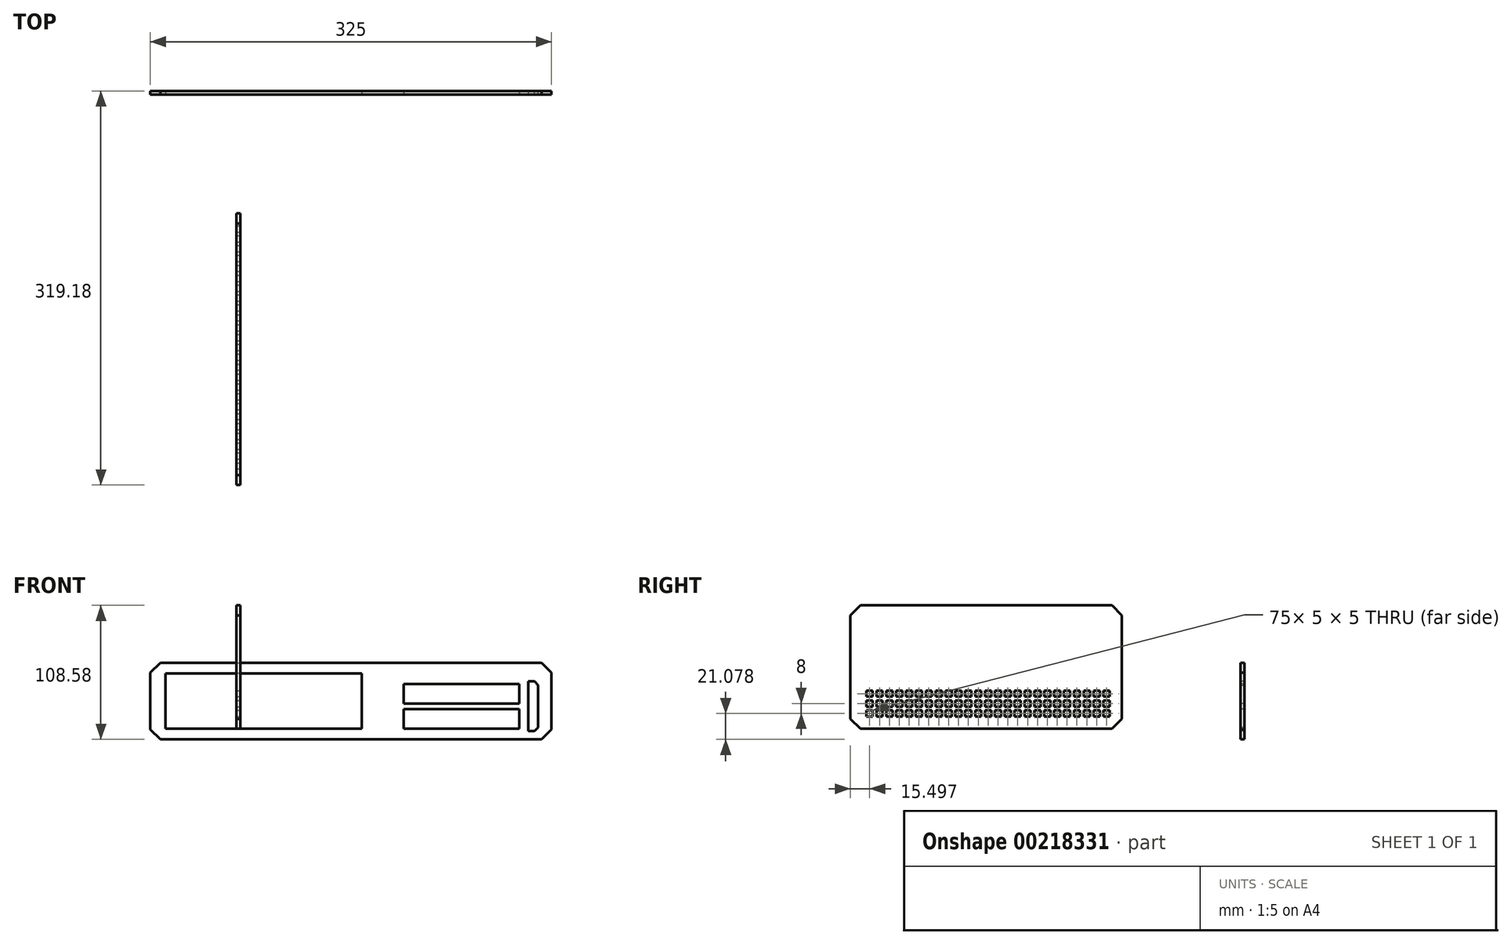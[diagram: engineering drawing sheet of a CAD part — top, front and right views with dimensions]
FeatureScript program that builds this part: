
annotation { "Feature Type Name" : "Feature", "Feature Type Description" : "" }
export const myFeature = defineFeature(function(context is Context, id is Id, definition is map)
    precondition{}
    {
        {
            var Q0;
            Q0=qCreatedBy(makeId("Front.planeOp"),FACE);
            var sketch = newSketch(context, id + "F0", { "sketchPlane" : qUnion([Q0])});
            skLineSegment(sketch, "E0.bottom", {"start": v(-69.82, 57.21) * mm, "end": v(255.18, 57.21) * mm});
            skLineSegment(sketch, "E0.top", {"start": v(-69.82, -4.79) * mm, "end": v(255.18, -4.79) * mm});
            skLineSegment(sketch, "E0.left", {"start": v(-69.82, 57.21) * mm, "end": v(-69.82, -4.79) * mm});
            skLineSegment(sketch, "E0.right", {"start": v(255.18, 57.21) * mm, "end": v(255.18, -4.79) * mm});
            skSolve(sketch);
        }
        {
            var Q0;
            Q0=makeQuery(id+"F0.imprint","IMPRINT",FACE,{"disambiguationData":[TD([[makeQuery(id+"F0.imprint","IMPRINT",EDGE,{"derivedFrom":sQuery(id+"F0.wireOp",EDGE,"E0.bottom")}),-1.0]])]});
            extrude(context, id + "F1", {"entities" : qUnion([Q0]), "depth" : 3 * mm});
        }
        {
            var Q0;
            Q0=qCreatedBy(makeId("Right.planeOp"),FACE);
            var sketch = newSketch(context, id + "F2", { "sketchPlane" : qUnion([Q0])});
            skLineSegment(sketch, "E1.bottom", {"start": v(-319.18, 103.79) * mm, "end": v(-99.18, 103.79) * mm});
            skLineSegment(sketch, "E1.top", {"start": v(-319.18, 3.79) * mm, "end": v(-99.18, 3.79) * mm});
            skLineSegment(sketch, "E1.left", {"start": v(-319.18, 103.79) * mm, "end": v(-319.18, 3.79) * mm});
            skLineSegment(sketch, "E1.right", {"start": v(-99.18, 103.79) * mm, "end": v(-99.18, 3.79) * mm});
            skSolve(sketch);
        }
        {
            var Q0;
            Q0=makeQuery(id+"F2.imprint","IMPRINT",FACE,{"disambiguationData":[TD([[makeQuery(id+"F2.imprint","IMPRINT",EDGE,{"derivedFrom":sQuery(id+"F2.wireOp",EDGE,"E1.bottom")}),-1.0]])]});
            extrude(context, id + "F3", {"entities" : qUnion([Q0]), "depth" : 3 * mm});
        }
        {
            var Q0;
            Q0=makeQuery(id+"F1.opExtrude","SWEPT_EDGE",EDGE,{"disambiguationData":[OSD([sQuery(id+"F0.wireOp",EDGE,"E0.bottom"),sQuery(id+"F0.wireOp",EDGE,"E0.left")])]});
            var Q1;
            Q1=makeQuery(id+"F1.opExtrude","SWEPT_EDGE",EDGE,{"disambiguationData":[OSD([sQuery(id+"F0.wireOp",EDGE,"E0.top"),sQuery(id+"F0.wireOp",EDGE,"E0.left")])]});
            var Q2;
            Q2=makeQuery(id+"F1.opExtrude","SWEPT_EDGE",EDGE,{"disambiguationData":[OSD([sQuery(id+"F0.wireOp",EDGE,"E0.bottom"),sQuery(id+"F0.wireOp",EDGE,"E0.right")])]});
            var Q3;
            Q3=makeQuery(id+"F1.opExtrude","SWEPT_EDGE",EDGE,{"disambiguationData":[OSD([sQuery(id+"F0.wireOp",EDGE,"E0.top"),sQuery(id+"F0.wireOp",EDGE,"E0.right")])]});
            var Q4;
            Q4=makeQuery(id+"F3.opExtrude","SWEPT_EDGE",EDGE,{"disambiguationData":[OSD([sQuery(id+"F2.wireOp",EDGE,"E1.bottom"),sQuery(id+"F2.wireOp",EDGE,"E1.left")])]});
            var Q5;
            Q5=makeQuery(id+"F3.opExtrude","SWEPT_EDGE",EDGE,{"disambiguationData":[OSD([sQuery(id+"F2.wireOp",EDGE,"E1.top"),sQuery(id+"F2.wireOp",EDGE,"E1.left")])]});
            var Q6;
            Q6=makeQuery(id+"F3.opExtrude","SWEPT_EDGE",EDGE,{"disambiguationData":[OSD([sQuery(id+"F2.wireOp",EDGE,"E1.top"),sQuery(id+"F2.wireOp",EDGE,"E1.right")])]});
            var Q7;
            Q7=makeQuery(id+"F3.opExtrude","SWEPT_EDGE",EDGE,{"disambiguationData":[OSD([sQuery(id+"F2.wireOp",EDGE,"E1.bottom"),sQuery(id+"F2.wireOp",EDGE,"E1.right")])]});
            chamfer(context, id + "F4", {"entities" : qUnion([Q0, Q1, Q2, Q3, Q4, Q5, Q6, Q7]), "width" : 8 * mm, "tangentPropagation" : true});
        }
        {
            var Q0;
            Q0=makeQuery(id+"F1.opExtrude","CAP_FACE",FACE,{"disambiguationData":[OSD([sQuery(id+"F0.wireOp",EDGE,"E0.bottom"),sQuery(id+"F0.wireOp",EDGE,"E0.top"),sQuery(id+"F0.wireOp",EDGE,"E0.left"),sQuery(id+"F0.wireOp",EDGE,"E0.right")])],"isStart":false});
            var sketch = newSketch(context, id + "F5", { "sketchPlane" : qUnion([Q0])});
            skLineSegment(sketch, "E2", {"start": v(-54.82, -4.79) * mm, "end": v(-54.82, 8.21) * mm, "construction": true});
            skLineSegment(sketch, "E3", {"start": v(-54.82, 8.21) * mm, "end": v(115.18, 8.21) * mm, "construction": true});
            skLineSegment(sketch, "E4", {"start": v(115.18, 8.21) * mm, "end": v(115.18, 4) * mm, "construction": true});
            skLineSegment(sketch, "E5", {"start": v(115.18, 4) * mm, "end": v(101.58, 4) * mm, "construction": true});
            skLineSegment(sketch, "E6.bottom", {"start": v(101.58, 4) * mm, "end": v(-57.42, 4) * mm});
            skLineSegment(sketch, "E6.top", {"start": v(101.58, 48.7) * mm, "end": v(-57.42, 48.7) * mm});
            skLineSegment(sketch, "E6.left", {"start": v(101.58, 4) * mm, "end": v(101.58, 48.7) * mm});
            skLineSegment(sketch, "E6.right", {"start": v(-57.42, 4) * mm, "end": v(-57.42, 48.7) * mm});
            skLineSegment(sketch, "E7", {"start": v(229.18, -4.79) * mm, "end": v(229.18, 40.21) * mm, "construction": true});
            skLineSegment(sketch, "E8.bottom", {"start": v(229.18, 40.21) * mm, "end": v(135.48, 40.21) * mm});
            skLineSegment(sketch, "E8.top", {"start": v(229.18, 24.31) * mm, "end": v(135.48, 24.31) * mm});
            skLineSegment(sketch, "E8.left", {"start": v(229.18, 40.21) * mm, "end": v(229.18, 24.31) * mm});
            skLineSegment(sketch, "E8.right", {"start": v(135.48, 40.21) * mm, "end": v(135.48, 24.31) * mm});
            skLineSegment(sketch, "E9.bottom", {"start": v(229.18, 19.91) * mm, "end": v(135.48, 19.91) * mm});
            skLineSegment(sketch, "E9.top", {"start": v(229.18, 4.01) * mm, "end": v(135.48, 4.01) * mm});
            skLineSegment(sketch, "E9.left", {"start": v(229.18, 19.91) * mm, "end": v(229.18, 4.01) * mm});
            skLineSegment(sketch, "E9.right", {"start": v(135.48, 19.91) * mm, "end": v(135.48, 4.01) * mm});
            skLineSegment(sketch, "E10", {"start": v(229.18, 40.21) * mm, "end": v(236.38, 40.21) * mm, "construction": true});
            skLineSegment(sketch, "E11", {"start": v(135.48, 40.21) * mm, "end": v(127.38, 40.21) * mm, "construction": true});
            skLineSegment(sketch, "E12", {"start": v(127.38, 40.21) * mm, "end": v(127.38, 4.01) * mm, "construction": true});
            skLineSegment(sketch, "E13", {"start": v(127.38, 4.01) * mm, "end": v(135.48, 4.01) * mm, "construction": true});
            skLineSegment(sketch, "E14", {"start": v(127.38, 40.21) * mm, "end": v(117.38, 40.21) * mm, "construction": true});
            skLineSegment(sketch, "E15", {"start": v(117.38, 40.21) * mm, "end": v(117.38, 4.01) * mm, "construction": true});
            skLineSegment(sketch, "E16", {"start": v(236.38, 40.21) * mm, "end": v(236.38, 2.01) * mm});
            skLineSegment(sketch, "E17", {"start": v(236.38, 40.21) * mm, "end": v(236.38, 42.21) * mm});
            skLineSegment(sketch, "E18", {"start": v(236.38, 42.21) * mm, "end": v(244.38, 42.21) * mm});
            skLineSegment(sketch, "E19", {"start": v(244.38, 42.21) * mm, "end": v(244.38, 2.01) * mm});
            skLineSegment(sketch, "E20", {"start": v(244.38, 2.01) * mm, "end": v(236.38, 2.01) * mm});
            skSolve(sketch);
        }
        {
            var Q0;
            Q0 = qSketchRegion(id + "F5", true);
            extrude(context, id + "F6", {"entities" : qUnion([Q0]), "operationType" : NewBodyOperationType.REMOVE, "oppositeDirection" : true, "depth" : 25 * mm});
        }
        {
            var Q0;
            Q0=makeQuery(id+"F6.boolean.opBoolean","COPY",EDGE,{"derivedFrom":makeQuery(id+"F6.opExtrude","SWEPT_EDGE",EDGE,{"disambiguationData":[OSD([sQuery(id+"F5.wireOp",EDGE,"E19"),sQuery(id+"F5.wireOp",EDGE,"E20")])]})});
            var Q1;
            Q1=makeQuery(id+"F6.boolean.opBoolean","COPY",EDGE,{"derivedFrom":makeQuery(id+"F6.opExtrude","SWEPT_EDGE",EDGE,{"disambiguationData":[OSD([sQuery(id+"F5.wireOp",EDGE,"E18"),sQuery(id+"F5.wireOp",EDGE,"E19")])]})});
            chamfer(context, id + "F7", {"entities" : qUnion([Q0, Q1]), "width" : 3 * mm, "tangentPropagation" : true});
        }
        {
            var Q0;
            Q0=makeQuery(id+"F3.opExtrude","CAP_FACE",FACE,{"disambiguationData":[OSD([sQuery(id+"F2.wireOp",EDGE,"E1.bottom"),sQuery(id+"F2.wireOp",EDGE,"E1.top"),sQuery(id+"F2.wireOp",EDGE,"E1.left"),sQuery(id+"F2.wireOp",EDGE,"E1.right")])],"isStart":false});
            var sketch = newSketch(context, id + "F8", { "sketchPlane" : qUnion([Q0])});
            skLineSegment(sketch, "E21.bottom", {"start": v(-306.18, 18.79) * mm, "end": v(-301.18, 18.79) * mm});
            skLineSegment(sketch, "E21.top", {"start": v(-306.18, 13.79) * mm, "end": v(-301.18, 13.79) * mm});
            skLineSegment(sketch, "E21.left", {"start": v(-306.18, 18.79) * mm, "end": v(-306.18, 13.79) * mm});
            skLineSegment(sketch, "E21.right", {"start": v(-301.18, 18.79) * mm, "end": v(-301.18, 13.79) * mm});
            skLineSegment(sketch, "E22", {"start": v(-306.18, 13.79) * mm, "end": v(-306.18, 3.79) * mm, "construction": true});
            skLineSegment(sketch, "E23.0.1.0", {"start": v(-301.18, 26.79) * mm, "end": v(-301.18, 21.79) * mm});
            skLineSegment(sketch, "E23.0.1.1", {"start": v(-306.18, 26.79) * mm, "end": v(-306.18, 21.79) * mm});
            skLineSegment(sketch, "E23.0.1.2", {"start": v(-306.18, 26.79) * mm, "end": v(-301.18, 26.79) * mm});
            skLineSegment(sketch, "E23.0.1.3", {"start": v(-306.18, 21.79) * mm, "end": v(-301.18, 21.79) * mm});
            skLineSegment(sketch, "E23.0.2.0", {"start": v(-301.18, 34.79) * mm, "end": v(-301.18, 29.79) * mm});
            skLineSegment(sketch, "E23.0.2.1", {"start": v(-306.18, 34.79) * mm, "end": v(-306.18, 29.79) * mm});
            skLineSegment(sketch, "E23.0.2.2", {"start": v(-306.18, 34.79) * mm, "end": v(-301.18, 34.79) * mm});
            skLineSegment(sketch, "E23.0.2.3", {"start": v(-306.18, 29.79) * mm, "end": v(-301.18, 29.79) * mm});
            skLineSegment(sketch, "E23.1.0.0", {"start": v(-293.18, 18.79) * mm, "end": v(-293.18, 13.79) * mm});
            skLineSegment(sketch, "E23.1.0.1", {"start": v(-298.18, 18.79) * mm, "end": v(-298.18, 13.79) * mm});
            skLineSegment(sketch, "E23.1.0.2", {"start": v(-298.18, 18.79) * mm, "end": v(-293.18, 18.79) * mm});
            skLineSegment(sketch, "E23.1.0.3", {"start": v(-298.18, 13.79) * mm, "end": v(-293.18, 13.79) * mm});
            skLineSegment(sketch, "E23.1.1.0", {"start": v(-293.18, 26.79) * mm, "end": v(-293.18, 21.79) * mm});
            skLineSegment(sketch, "E23.1.1.1", {"start": v(-298.18, 26.79) * mm, "end": v(-298.18, 21.79) * mm});
            skLineSegment(sketch, "E23.1.1.2", {"start": v(-298.18, 26.79) * mm, "end": v(-293.18, 26.79) * mm});
            skLineSegment(sketch, "E23.1.1.3", {"start": v(-298.18, 21.79) * mm, "end": v(-293.18, 21.79) * mm});
            skLineSegment(sketch, "E23.1.2.0", {"start": v(-293.18, 34.79) * mm, "end": v(-293.18, 29.79) * mm});
            skLineSegment(sketch, "E23.1.2.1", {"start": v(-298.18, 34.79) * mm, "end": v(-298.18, 29.79) * mm});
            skLineSegment(sketch, "E23.1.2.2", {"start": v(-298.18, 34.79) * mm, "end": v(-293.18, 34.79) * mm});
            skLineSegment(sketch, "E23.1.2.3", {"start": v(-298.18, 29.79) * mm, "end": v(-293.18, 29.79) * mm});
            skLineSegment(sketch, "E23.2.0.0", {"start": v(-285.18, 18.79) * mm, "end": v(-285.18, 13.79) * mm});
            skLineSegment(sketch, "E23.2.0.1", {"start": v(-290.18, 18.79) * mm, "end": v(-290.18, 13.79) * mm});
            skLineSegment(sketch, "E23.2.0.2", {"start": v(-290.18, 18.79) * mm, "end": v(-285.18, 18.79) * mm});
            skLineSegment(sketch, "E23.2.0.3", {"start": v(-290.18, 13.79) * mm, "end": v(-285.18, 13.79) * mm});
            skLineSegment(sketch, "E23.2.1.0", {"start": v(-285.18, 26.79) * mm, "end": v(-285.18, 21.79) * mm});
            skLineSegment(sketch, "E23.2.1.1", {"start": v(-290.18, 26.79) * mm, "end": v(-290.18, 21.79) * mm});
            skLineSegment(sketch, "E23.2.1.2", {"start": v(-290.18, 26.79) * mm, "end": v(-285.18, 26.79) * mm});
            skLineSegment(sketch, "E23.2.1.3", {"start": v(-290.18, 21.79) * mm, "end": v(-285.18, 21.79) * mm});
            skLineSegment(sketch, "E23.2.2.0", {"start": v(-285.18, 34.79) * mm, "end": v(-285.18, 29.79) * mm});
            skLineSegment(sketch, "E23.2.2.1", {"start": v(-290.18, 34.79) * mm, "end": v(-290.18, 29.79) * mm});
            skLineSegment(sketch, "E23.2.2.2", {"start": v(-290.18, 34.79) * mm, "end": v(-285.18, 34.79) * mm});
            skLineSegment(sketch, "E23.2.2.3", {"start": v(-290.18, 29.79) * mm, "end": v(-285.18, 29.79) * mm});
            skLineSegment(sketch, "E23.3.0.0", {"start": v(-277.18, 18.79) * mm, "end": v(-277.18, 13.79) * mm});
            skLineSegment(sketch, "E23.3.0.1", {"start": v(-282.18, 18.79) * mm, "end": v(-282.18, 13.79) * mm});
            skLineSegment(sketch, "E23.3.0.2", {"start": v(-282.18, 18.79) * mm, "end": v(-277.18, 18.79) * mm});
            skLineSegment(sketch, "E23.3.0.3", {"start": v(-282.18, 13.79) * mm, "end": v(-277.18, 13.79) * mm});
            skLineSegment(sketch, "E23.3.1.0", {"start": v(-277.18, 26.79) * mm, "end": v(-277.18, 21.79) * mm});
            skLineSegment(sketch, "E23.3.1.1", {"start": v(-282.18, 26.79) * mm, "end": v(-282.18, 21.79) * mm});
            skLineSegment(sketch, "E23.3.1.2", {"start": v(-282.18, 26.79) * mm, "end": v(-277.18, 26.79) * mm});
            skLineSegment(sketch, "E23.3.1.3", {"start": v(-282.18, 21.79) * mm, "end": v(-277.18, 21.79) * mm});
            skLineSegment(sketch, "E23.3.2.0", {"start": v(-277.18, 34.79) * mm, "end": v(-277.18, 29.79) * mm});
            skLineSegment(sketch, "E23.3.2.1", {"start": v(-282.18, 34.79) * mm, "end": v(-282.18, 29.79) * mm});
            skLineSegment(sketch, "E23.3.2.2", {"start": v(-282.18, 34.79) * mm, "end": v(-277.18, 34.79) * mm});
            skLineSegment(sketch, "E23.3.2.3", {"start": v(-282.18, 29.79) * mm, "end": v(-277.18, 29.79) * mm});
            skLineSegment(sketch, "E23.4.0.0", {"start": v(-269.18, 18.79) * mm, "end": v(-269.18, 13.79) * mm});
            skLineSegment(sketch, "E23.4.0.1", {"start": v(-274.18, 18.79) * mm, "end": v(-274.18, 13.79) * mm});
            skLineSegment(sketch, "E23.4.0.2", {"start": v(-274.18, 18.79) * mm, "end": v(-269.18, 18.79) * mm});
            skLineSegment(sketch, "E23.4.0.3", {"start": v(-274.18, 13.79) * mm, "end": v(-269.18, 13.79) * mm});
            skLineSegment(sketch, "E23.4.1.0", {"start": v(-269.18, 26.79) * mm, "end": v(-269.18, 21.79) * mm});
            skLineSegment(sketch, "E23.4.1.1", {"start": v(-274.18, 26.79) * mm, "end": v(-274.18, 21.79) * mm});
            skLineSegment(sketch, "E23.4.1.2", {"start": v(-274.18, 26.79) * mm, "end": v(-269.18, 26.79) * mm});
            skLineSegment(sketch, "E23.4.1.3", {"start": v(-274.18, 21.79) * mm, "end": v(-269.18, 21.79) * mm});
            skLineSegment(sketch, "E23.4.2.0", {"start": v(-269.18, 34.79) * mm, "end": v(-269.18, 29.79) * mm});
            skLineSegment(sketch, "E23.4.2.1", {"start": v(-274.18, 34.79) * mm, "end": v(-274.18, 29.79) * mm});
            skLineSegment(sketch, "E23.4.2.2", {"start": v(-274.18, 34.79) * mm, "end": v(-269.18, 34.79) * mm});
            skLineSegment(sketch, "E23.4.2.3", {"start": v(-274.18, 29.79) * mm, "end": v(-269.18, 29.79) * mm});
            skLineSegment(sketch, "E23.5.0.0", {"start": v(-261.18, 18.79) * mm, "end": v(-261.18, 13.79) * mm});
            skLineSegment(sketch, "E23.5.0.1", {"start": v(-266.18, 18.79) * mm, "end": v(-266.18, 13.79) * mm});
            skLineSegment(sketch, "E23.5.0.2", {"start": v(-266.18, 18.79) * mm, "end": v(-261.18, 18.79) * mm});
            skLineSegment(sketch, "E23.5.0.3", {"start": v(-266.18, 13.79) * mm, "end": v(-261.18, 13.79) * mm});
            skLineSegment(sketch, "E23.5.1.0", {"start": v(-261.18, 26.79) * mm, "end": v(-261.18, 21.79) * mm});
            skLineSegment(sketch, "E23.5.1.1", {"start": v(-266.18, 26.79) * mm, "end": v(-266.18, 21.79) * mm});
            skLineSegment(sketch, "E23.5.1.2", {"start": v(-266.18, 26.79) * mm, "end": v(-261.18, 26.79) * mm});
            skLineSegment(sketch, "E23.5.1.3", {"start": v(-266.18, 21.79) * mm, "end": v(-261.18, 21.79) * mm});
            skLineSegment(sketch, "E23.5.2.0", {"start": v(-261.18, 34.79) * mm, "end": v(-261.18, 29.79) * mm});
            skLineSegment(sketch, "E23.5.2.1", {"start": v(-266.18, 34.79) * mm, "end": v(-266.18, 29.79) * mm});
            skLineSegment(sketch, "E23.5.2.2", {"start": v(-266.18, 34.79) * mm, "end": v(-261.18, 34.79) * mm});
            skLineSegment(sketch, "E23.5.2.3", {"start": v(-266.18, 29.79) * mm, "end": v(-261.18, 29.79) * mm});
            skLineSegment(sketch, "E23.6.0.0", {"start": v(-253.18, 18.79) * mm, "end": v(-253.18, 13.79) * mm});
            skLineSegment(sketch, "E23.6.0.1", {"start": v(-258.18, 18.79) * mm, "end": v(-258.18, 13.79) * mm});
            skLineSegment(sketch, "E23.6.0.2", {"start": v(-258.18, 18.79) * mm, "end": v(-253.18, 18.79) * mm});
            skLineSegment(sketch, "E23.6.0.3", {"start": v(-258.18, 13.79) * mm, "end": v(-253.18, 13.79) * mm});
            skLineSegment(sketch, "E23.6.1.0", {"start": v(-253.18, 26.79) * mm, "end": v(-253.18, 21.79) * mm});
            skLineSegment(sketch, "E23.6.1.1", {"start": v(-258.18, 26.79) * mm, "end": v(-258.18, 21.79) * mm});
            skLineSegment(sketch, "E23.6.1.2", {"start": v(-258.18, 26.79) * mm, "end": v(-253.18, 26.79) * mm});
            skLineSegment(sketch, "E23.6.1.3", {"start": v(-258.18, 21.79) * mm, "end": v(-253.18, 21.79) * mm});
            skLineSegment(sketch, "E23.6.2.0", {"start": v(-253.18, 34.79) * mm, "end": v(-253.18, 29.79) * mm});
            skLineSegment(sketch, "E23.6.2.1", {"start": v(-258.18, 34.79) * mm, "end": v(-258.18, 29.79) * mm});
            skLineSegment(sketch, "E23.6.2.2", {"start": v(-258.18, 34.79) * mm, "end": v(-253.18, 34.79) * mm});
            skLineSegment(sketch, "E23.6.2.3", {"start": v(-258.18, 29.79) * mm, "end": v(-253.18, 29.79) * mm});
            skLineSegment(sketch, "E23.7.0.0", {"start": v(-245.18, 18.79) * mm, "end": v(-245.18, 13.79) * mm});
            skLineSegment(sketch, "E23.7.0.1", {"start": v(-250.18, 18.79) * mm, "end": v(-250.18, 13.79) * mm});
            skLineSegment(sketch, "E23.7.0.2", {"start": v(-250.18, 18.79) * mm, "end": v(-245.18, 18.79) * mm});
            skLineSegment(sketch, "E23.7.0.3", {"start": v(-250.18, 13.79) * mm, "end": v(-245.18, 13.79) * mm});
            skLineSegment(sketch, "E23.7.1.0", {"start": v(-245.18, 26.79) * mm, "end": v(-245.18, 21.79) * mm});
            skLineSegment(sketch, "E23.7.1.1", {"start": v(-250.18, 26.79) * mm, "end": v(-250.18, 21.79) * mm});
            skLineSegment(sketch, "E23.7.1.2", {"start": v(-250.18, 26.79) * mm, "end": v(-245.18, 26.79) * mm});
            skLineSegment(sketch, "E23.7.1.3", {"start": v(-250.18, 21.79) * mm, "end": v(-245.18, 21.79) * mm});
            skLineSegment(sketch, "E23.7.2.0", {"start": v(-245.18, 34.79) * mm, "end": v(-245.18, 29.79) * mm});
            skLineSegment(sketch, "E23.7.2.1", {"start": v(-250.18, 34.79) * mm, "end": v(-250.18, 29.79) * mm});
            skLineSegment(sketch, "E23.7.2.2", {"start": v(-250.18, 34.79) * mm, "end": v(-245.18, 34.79) * mm});
            skLineSegment(sketch, "E23.7.2.3", {"start": v(-250.18, 29.79) * mm, "end": v(-245.18, 29.79) * mm});
            skLineSegment(sketch, "E23.8.0.0", {"start": v(-237.18, 18.79) * mm, "end": v(-237.18, 13.79) * mm});
            skLineSegment(sketch, "E23.8.0.1", {"start": v(-242.18, 18.79) * mm, "end": v(-242.18, 13.79) * mm});
            skLineSegment(sketch, "E23.8.0.2", {"start": v(-242.18, 18.79) * mm, "end": v(-237.18, 18.79) * mm});
            skLineSegment(sketch, "E23.8.0.3", {"start": v(-242.18, 13.79) * mm, "end": v(-237.18, 13.79) * mm});
            skLineSegment(sketch, "E23.8.1.0", {"start": v(-237.18, 26.79) * mm, "end": v(-237.18, 21.79) * mm});
            skLineSegment(sketch, "E23.8.1.1", {"start": v(-242.18, 26.79) * mm, "end": v(-242.18, 21.79) * mm});
            skLineSegment(sketch, "E23.8.1.2", {"start": v(-242.18, 26.79) * mm, "end": v(-237.18, 26.79) * mm});
            skLineSegment(sketch, "E23.8.1.3", {"start": v(-242.18, 21.79) * mm, "end": v(-237.18, 21.79) * mm});
            skLineSegment(sketch, "E23.8.2.0", {"start": v(-237.18, 34.79) * mm, "end": v(-237.18, 29.79) * mm});
            skLineSegment(sketch, "E23.8.2.1", {"start": v(-242.18, 34.79) * mm, "end": v(-242.18, 29.79) * mm});
            skLineSegment(sketch, "E23.8.2.2", {"start": v(-242.18, 34.79) * mm, "end": v(-237.18, 34.79) * mm});
            skLineSegment(sketch, "E23.8.2.3", {"start": v(-242.18, 29.79) * mm, "end": v(-237.18, 29.79) * mm});
            skLineSegment(sketch, "E23.9.0.0", {"start": v(-229.18, 18.79) * mm, "end": v(-229.18, 13.79) * mm});
            skLineSegment(sketch, "E23.9.0.1", {"start": v(-234.18, 18.79) * mm, "end": v(-234.18, 13.79) * mm});
            skLineSegment(sketch, "E23.9.0.2", {"start": v(-234.18, 18.79) * mm, "end": v(-229.18, 18.79) * mm});
            skLineSegment(sketch, "E23.9.0.3", {"start": v(-234.18, 13.79) * mm, "end": v(-229.18, 13.79) * mm});
            skLineSegment(sketch, "E23.9.1.0", {"start": v(-229.18, 26.79) * mm, "end": v(-229.18, 21.79) * mm});
            skLineSegment(sketch, "E23.9.1.1", {"start": v(-234.18, 26.79) * mm, "end": v(-234.18, 21.79) * mm});
            skLineSegment(sketch, "E23.9.1.2", {"start": v(-234.18, 26.79) * mm, "end": v(-229.18, 26.79) * mm});
            skLineSegment(sketch, "E23.9.1.3", {"start": v(-234.18, 21.79) * mm, "end": v(-229.18, 21.79) * mm});
            skLineSegment(sketch, "E23.9.2.0", {"start": v(-229.18, 34.79) * mm, "end": v(-229.18, 29.79) * mm});
            skLineSegment(sketch, "E23.9.2.1", {"start": v(-234.18, 34.79) * mm, "end": v(-234.18, 29.79) * mm});
            skLineSegment(sketch, "E23.9.2.2", {"start": v(-234.18, 34.79) * mm, "end": v(-229.18, 34.79) * mm});
            skLineSegment(sketch, "E23.9.2.3", {"start": v(-234.18, 29.79) * mm, "end": v(-229.18, 29.79) * mm});
            skLineSegment(sketch, "E23.10.0.0", {"start": v(-221.18, 18.79) * mm, "end": v(-221.18, 13.79) * mm});
            skLineSegment(sketch, "E23.10.0.1", {"start": v(-226.18, 18.79) * mm, "end": v(-226.18, 13.79) * mm});
            skLineSegment(sketch, "E23.10.0.2", {"start": v(-226.18, 18.79) * mm, "end": v(-221.18, 18.79) * mm});
            skLineSegment(sketch, "E23.10.0.3", {"start": v(-226.18, 13.79) * mm, "end": v(-221.18, 13.79) * mm});
            skLineSegment(sketch, "E23.10.1.0", {"start": v(-221.18, 26.79) * mm, "end": v(-221.18, 21.79) * mm});
            skLineSegment(sketch, "E23.10.1.1", {"start": v(-226.18, 26.79) * mm, "end": v(-226.18, 21.79) * mm});
            skLineSegment(sketch, "E23.10.1.2", {"start": v(-226.18, 26.79) * mm, "end": v(-221.18, 26.79) * mm});
            skLineSegment(sketch, "E23.10.1.3", {"start": v(-226.18, 21.79) * mm, "end": v(-221.18, 21.79) * mm});
            skLineSegment(sketch, "E23.10.2.0", {"start": v(-221.18, 34.79) * mm, "end": v(-221.18, 29.79) * mm});
            skLineSegment(sketch, "E23.10.2.1", {"start": v(-226.18, 34.79) * mm, "end": v(-226.18, 29.79) * mm});
            skLineSegment(sketch, "E23.10.2.2", {"start": v(-226.18, 34.79) * mm, "end": v(-221.18, 34.79) * mm});
            skLineSegment(sketch, "E23.10.2.3", {"start": v(-226.18, 29.79) * mm, "end": v(-221.18, 29.79) * mm});
            skLineSegment(sketch, "E23.11.0.0", {"start": v(-213.18, 18.79) * mm, "end": v(-213.18, 13.79) * mm});
            skLineSegment(sketch, "E23.11.0.1", {"start": v(-218.18, 18.79) * mm, "end": v(-218.18, 13.79) * mm});
            skLineSegment(sketch, "E23.11.0.2", {"start": v(-218.18, 18.79) * mm, "end": v(-213.18, 18.79) * mm});
            skLineSegment(sketch, "E23.11.0.3", {"start": v(-218.18, 13.79) * mm, "end": v(-213.18, 13.79) * mm});
            skLineSegment(sketch, "E23.11.1.0", {"start": v(-213.18, 26.79) * mm, "end": v(-213.18, 21.79) * mm});
            skLineSegment(sketch, "E23.11.1.1", {"start": v(-218.18, 26.79) * mm, "end": v(-218.18, 21.79) * mm});
            skLineSegment(sketch, "E23.11.1.2", {"start": v(-218.18, 26.79) * mm, "end": v(-213.18, 26.79) * mm});
            skLineSegment(sketch, "E23.11.1.3", {"start": v(-218.18, 21.79) * mm, "end": v(-213.18, 21.79) * mm});
            skLineSegment(sketch, "E23.11.2.0", {"start": v(-213.18, 34.79) * mm, "end": v(-213.18, 29.79) * mm});
            skLineSegment(sketch, "E23.11.2.1", {"start": v(-218.18, 34.79) * mm, "end": v(-218.18, 29.79) * mm});
            skLineSegment(sketch, "E23.11.2.2", {"start": v(-218.18, 34.79) * mm, "end": v(-213.18, 34.79) * mm});
            skLineSegment(sketch, "E23.11.2.3", {"start": v(-218.18, 29.79) * mm, "end": v(-213.18, 29.79) * mm});
            skLineSegment(sketch, "E23.12.0.0", {"start": v(-205.18, 18.79) * mm, "end": v(-205.18, 13.79) * mm});
            skLineSegment(sketch, "E23.12.0.1", {"start": v(-210.18, 18.79) * mm, "end": v(-210.18, 13.79) * mm});
            skLineSegment(sketch, "E23.12.0.2", {"start": v(-210.18, 18.79) * mm, "end": v(-205.18, 18.79) * mm});
            skLineSegment(sketch, "E23.12.0.3", {"start": v(-210.18, 13.79) * mm, "end": v(-205.18, 13.79) * mm});
            skLineSegment(sketch, "E23.12.1.0", {"start": v(-205.18, 26.79) * mm, "end": v(-205.18, 21.79) * mm});
            skLineSegment(sketch, "E23.12.1.1", {"start": v(-210.18, 26.79) * mm, "end": v(-210.18, 21.79) * mm});
            skLineSegment(sketch, "E23.12.1.2", {"start": v(-210.18, 26.79) * mm, "end": v(-205.18, 26.79) * mm});
            skLineSegment(sketch, "E23.12.1.3", {"start": v(-210.18, 21.79) * mm, "end": v(-205.18, 21.79) * mm});
            skLineSegment(sketch, "E23.12.2.0", {"start": v(-205.18, 34.79) * mm, "end": v(-205.18, 29.79) * mm});
            skLineSegment(sketch, "E23.12.2.1", {"start": v(-210.18, 34.79) * mm, "end": v(-210.18, 29.79) * mm});
            skLineSegment(sketch, "E23.12.2.2", {"start": v(-210.18, 34.79) * mm, "end": v(-205.18, 34.79) * mm});
            skLineSegment(sketch, "E23.12.2.3", {"start": v(-210.18, 29.79) * mm, "end": v(-205.18, 29.79) * mm});
            skLineSegment(sketch, "E23.13.0.0", {"start": v(-197.18, 18.79) * mm, "end": v(-197.18, 13.79) * mm});
            skLineSegment(sketch, "E23.13.0.1", {"start": v(-202.18, 18.79) * mm, "end": v(-202.18, 13.79) * mm});
            skLineSegment(sketch, "E23.13.0.2", {"start": v(-202.18, 18.79) * mm, "end": v(-197.18, 18.79) * mm});
            skLineSegment(sketch, "E23.13.0.3", {"start": v(-202.18, 13.79) * mm, "end": v(-197.18, 13.79) * mm});
            skLineSegment(sketch, "E23.13.1.0", {"start": v(-197.18, 26.79) * mm, "end": v(-197.18, 21.79) * mm});
            skLineSegment(sketch, "E23.13.1.1", {"start": v(-202.18, 26.79) * mm, "end": v(-202.18, 21.79) * mm});
            skLineSegment(sketch, "E23.13.1.2", {"start": v(-202.18, 26.79) * mm, "end": v(-197.18, 26.79) * mm});
            skLineSegment(sketch, "E23.13.1.3", {"start": v(-202.18, 21.79) * mm, "end": v(-197.18, 21.79) * mm});
            skLineSegment(sketch, "E23.13.2.0", {"start": v(-197.18, 34.79) * mm, "end": v(-197.18, 29.79) * mm});
            skLineSegment(sketch, "E23.13.2.1", {"start": v(-202.18, 34.79) * mm, "end": v(-202.18, 29.79) * mm});
            skLineSegment(sketch, "E23.13.2.2", {"start": v(-202.18, 34.79) * mm, "end": v(-197.18, 34.79) * mm});
            skLineSegment(sketch, "E23.13.2.3", {"start": v(-202.18, 29.79) * mm, "end": v(-197.18, 29.79) * mm});
            skLineSegment(sketch, "E23.14.0.0", {"start": v(-189.18, 18.79) * mm, "end": v(-189.18, 13.79) * mm});
            skLineSegment(sketch, "E23.14.0.1", {"start": v(-194.18, 18.79) * mm, "end": v(-194.18, 13.79) * mm});
            skLineSegment(sketch, "E23.14.0.2", {"start": v(-194.18, 18.79) * mm, "end": v(-189.18, 18.79) * mm});
            skLineSegment(sketch, "E23.14.0.3", {"start": v(-194.18, 13.79) * mm, "end": v(-189.18, 13.79) * mm});
            skLineSegment(sketch, "E23.14.1.0", {"start": v(-189.18, 26.79) * mm, "end": v(-189.18, 21.79) * mm});
            skLineSegment(sketch, "E23.14.1.1", {"start": v(-194.18, 26.79) * mm, "end": v(-194.18, 21.79) * mm});
            skLineSegment(sketch, "E23.14.1.2", {"start": v(-194.18, 26.79) * mm, "end": v(-189.18, 26.79) * mm});
            skLineSegment(sketch, "E23.14.1.3", {"start": v(-194.18, 21.79) * mm, "end": v(-189.18, 21.79) * mm});
            skLineSegment(sketch, "E23.14.2.0", {"start": v(-189.18, 34.79) * mm, "end": v(-189.18, 29.79) * mm});
            skLineSegment(sketch, "E23.14.2.1", {"start": v(-194.18, 34.79) * mm, "end": v(-194.18, 29.79) * mm});
            skLineSegment(sketch, "E23.14.2.2", {"start": v(-194.18, 34.79) * mm, "end": v(-189.18, 34.79) * mm});
            skLineSegment(sketch, "E23.14.2.3", {"start": v(-194.18, 29.79) * mm, "end": v(-189.18, 29.79) * mm});
            skLineSegment(sketch, "E23.15.0.0", {"start": v(-181.18, 18.79) * mm, "end": v(-181.18, 13.79) * mm});
            skLineSegment(sketch, "E23.15.0.1", {"start": v(-186.18, 18.79) * mm, "end": v(-186.18, 13.79) * mm});
            skLineSegment(sketch, "E23.15.0.2", {"start": v(-186.18, 18.79) * mm, "end": v(-181.18, 18.79) * mm});
            skLineSegment(sketch, "E23.15.0.3", {"start": v(-186.18, 13.79) * mm, "end": v(-181.18, 13.79) * mm});
            skLineSegment(sketch, "E23.15.1.0", {"start": v(-181.18, 26.79) * mm, "end": v(-181.18, 21.79) * mm});
            skLineSegment(sketch, "E23.15.1.1", {"start": v(-186.18, 26.79) * mm, "end": v(-186.18, 21.79) * mm});
            skLineSegment(sketch, "E23.15.1.2", {"start": v(-186.18, 26.79) * mm, "end": v(-181.18, 26.79) * mm});
            skLineSegment(sketch, "E23.15.1.3", {"start": v(-186.18, 21.79) * mm, "end": v(-181.18, 21.79) * mm});
            skLineSegment(sketch, "E23.15.2.0", {"start": v(-181.18, 34.79) * mm, "end": v(-181.18, 29.79) * mm});
            skLineSegment(sketch, "E23.15.2.1", {"start": v(-186.18, 34.79) * mm, "end": v(-186.18, 29.79) * mm});
            skLineSegment(sketch, "E23.15.2.2", {"start": v(-186.18, 34.79) * mm, "end": v(-181.18, 34.79) * mm});
            skLineSegment(sketch, "E23.15.2.3", {"start": v(-186.18, 29.79) * mm, "end": v(-181.18, 29.79) * mm});
            skLineSegment(sketch, "E23.16.0.0", {"start": v(-173.18, 18.79) * mm, "end": v(-173.18, 13.79) * mm});
            skLineSegment(sketch, "E23.16.0.1", {"start": v(-178.18, 18.79) * mm, "end": v(-178.18, 13.79) * mm});
            skLineSegment(sketch, "E23.16.0.2", {"start": v(-178.18, 18.79) * mm, "end": v(-173.18, 18.79) * mm});
            skLineSegment(sketch, "E23.16.0.3", {"start": v(-178.18, 13.79) * mm, "end": v(-173.18, 13.79) * mm});
            skLineSegment(sketch, "E23.16.1.0", {"start": v(-173.18, 26.79) * mm, "end": v(-173.18, 21.79) * mm});
            skLineSegment(sketch, "E23.16.1.1", {"start": v(-178.18, 26.79) * mm, "end": v(-178.18, 21.79) * mm});
            skLineSegment(sketch, "E23.16.1.2", {"start": v(-178.18, 26.79) * mm, "end": v(-173.18, 26.79) * mm});
            skLineSegment(sketch, "E23.16.1.3", {"start": v(-178.18, 21.79) * mm, "end": v(-173.18, 21.79) * mm});
            skLineSegment(sketch, "E23.16.2.0", {"start": v(-173.18, 34.79) * mm, "end": v(-173.18, 29.79) * mm});
            skLineSegment(sketch, "E23.16.2.1", {"start": v(-178.18, 34.79) * mm, "end": v(-178.18, 29.79) * mm});
            skLineSegment(sketch, "E23.16.2.2", {"start": v(-178.18, 34.79) * mm, "end": v(-173.18, 34.79) * mm});
            skLineSegment(sketch, "E23.16.2.3", {"start": v(-178.18, 29.79) * mm, "end": v(-173.18, 29.79) * mm});
            skLineSegment(sketch, "E23.17.0.0", {"start": v(-165.18, 18.79) * mm, "end": v(-165.18, 13.79) * mm});
            skLineSegment(sketch, "E23.17.0.1", {"start": v(-170.18, 18.79) * mm, "end": v(-170.18, 13.79) * mm});
            skLineSegment(sketch, "E23.17.0.2", {"start": v(-170.18, 18.79) * mm, "end": v(-165.18, 18.79) * mm});
            skLineSegment(sketch, "E23.17.0.3", {"start": v(-170.18, 13.79) * mm, "end": v(-165.18, 13.79) * mm});
            skLineSegment(sketch, "E23.17.1.0", {"start": v(-165.18, 26.79) * mm, "end": v(-165.18, 21.79) * mm});
            skLineSegment(sketch, "E23.17.1.1", {"start": v(-170.18, 26.79) * mm, "end": v(-170.18, 21.79) * mm});
            skLineSegment(sketch, "E23.17.1.2", {"start": v(-170.18, 26.79) * mm, "end": v(-165.18, 26.79) * mm});
            skLineSegment(sketch, "E23.17.1.3", {"start": v(-170.18, 21.79) * mm, "end": v(-165.18, 21.79) * mm});
            skLineSegment(sketch, "E23.17.2.0", {"start": v(-165.18, 34.79) * mm, "end": v(-165.18, 29.79) * mm});
            skLineSegment(sketch, "E23.17.2.1", {"start": v(-170.18, 34.79) * mm, "end": v(-170.18, 29.79) * mm});
            skLineSegment(sketch, "E23.17.2.2", {"start": v(-170.18, 34.79) * mm, "end": v(-165.18, 34.79) * mm});
            skLineSegment(sketch, "E23.17.2.3", {"start": v(-170.18, 29.79) * mm, "end": v(-165.18, 29.79) * mm});
            skLineSegment(sketch, "E23.18.0.0", {"start": v(-157.18, 18.79) * mm, "end": v(-157.18, 13.79) * mm});
            skLineSegment(sketch, "E23.18.0.1", {"start": v(-162.18, 18.79) * mm, "end": v(-162.18, 13.79) * mm});
            skLineSegment(sketch, "E23.18.0.2", {"start": v(-162.18, 18.79) * mm, "end": v(-157.18, 18.79) * mm});
            skLineSegment(sketch, "E23.18.0.3", {"start": v(-162.18, 13.79) * mm, "end": v(-157.18, 13.79) * mm});
            skLineSegment(sketch, "E23.18.1.0", {"start": v(-157.18, 26.79) * mm, "end": v(-157.18, 21.79) * mm});
            skLineSegment(sketch, "E23.18.1.1", {"start": v(-162.18, 26.79) * mm, "end": v(-162.18, 21.79) * mm});
            skLineSegment(sketch, "E23.18.1.2", {"start": v(-162.18, 26.79) * mm, "end": v(-157.18, 26.79) * mm});
            skLineSegment(sketch, "E23.18.1.3", {"start": v(-162.18, 21.79) * mm, "end": v(-157.18, 21.79) * mm});
            skLineSegment(sketch, "E23.18.2.0", {"start": v(-157.18, 34.79) * mm, "end": v(-157.18, 29.79) * mm});
            skLineSegment(sketch, "E23.18.2.1", {"start": v(-162.18, 34.79) * mm, "end": v(-162.18, 29.79) * mm});
            skLineSegment(sketch, "E23.18.2.2", {"start": v(-162.18, 34.79) * mm, "end": v(-157.18, 34.79) * mm});
            skLineSegment(sketch, "E23.18.2.3", {"start": v(-162.18, 29.79) * mm, "end": v(-157.18, 29.79) * mm});
            skLineSegment(sketch, "E23.19.0.0", {"start": v(-149.18, 18.79) * mm, "end": v(-149.18, 13.79) * mm});
            skLineSegment(sketch, "E23.19.0.1", {"start": v(-154.18, 18.79) * mm, "end": v(-154.18, 13.79) * mm});
            skLineSegment(sketch, "E23.19.0.2", {"start": v(-154.18, 18.79) * mm, "end": v(-149.18, 18.79) * mm});
            skLineSegment(sketch, "E23.19.0.3", {"start": v(-154.18, 13.79) * mm, "end": v(-149.18, 13.79) * mm});
            skLineSegment(sketch, "E23.19.1.0", {"start": v(-149.18, 26.79) * mm, "end": v(-149.18, 21.79) * mm});
            skLineSegment(sketch, "E23.19.1.1", {"start": v(-154.18, 26.79) * mm, "end": v(-154.18, 21.79) * mm});
            skLineSegment(sketch, "E23.19.1.2", {"start": v(-154.18, 26.79) * mm, "end": v(-149.18, 26.79) * mm});
            skLineSegment(sketch, "E23.19.1.3", {"start": v(-154.18, 21.79) * mm, "end": v(-149.18, 21.79) * mm});
            skLineSegment(sketch, "E23.19.2.0", {"start": v(-149.18, 34.79) * mm, "end": v(-149.18, 29.79) * mm});
            skLineSegment(sketch, "E23.19.2.1", {"start": v(-154.18, 34.79) * mm, "end": v(-154.18, 29.79) * mm});
            skLineSegment(sketch, "E23.19.2.2", {"start": v(-154.18, 34.79) * mm, "end": v(-149.18, 34.79) * mm});
            skLineSegment(sketch, "E23.19.2.3", {"start": v(-154.18, 29.79) * mm, "end": v(-149.18, 29.79) * mm});
            skLineSegment(sketch, "E23.direction1", {"start": v(-306.18, 13.79) * mm, "end": v(-298.18, 13.79) * mm, "construction": true});
            skLineSegment(sketch, "E23.direction2", {"start": v(-306.18, 13.79) * mm, "end": v(-306.18, 21.79) * mm, "construction": true});
            skLineSegment(sketch, "E24.0.20.0", {"start": v(-141.18, 18.79) * mm, "end": v(-141.18, 13.79) * mm});
            skLineSegment(sketch, "E24.3.20.0", {"start": v(-146.18, 18.79) * mm, "end": v(-146.18, 13.79) * mm});
            skLineSegment(sketch, "E24.6.20.0", {"start": v(-146.18, 18.79) * mm, "end": v(-141.18, 18.79) * mm});
            skLineSegment(sketch, "E24.9.20.0", {"start": v(-146.18, 13.79) * mm, "end": v(-141.18, 13.79) * mm});
            skLineSegment(sketch, "E24.0.20.1", {"start": v(-141.18, 26.79) * mm, "end": v(-141.18, 21.79) * mm});
            skLineSegment(sketch, "E24.3.20.1", {"start": v(-146.18, 26.79) * mm, "end": v(-146.18, 21.79) * mm});
            skLineSegment(sketch, "E24.6.20.1", {"start": v(-146.18, 26.79) * mm, "end": v(-141.18, 26.79) * mm});
            skLineSegment(sketch, "E24.9.20.1", {"start": v(-146.18, 21.79) * mm, "end": v(-141.18, 21.79) * mm});
            skLineSegment(sketch, "E24.0.20.2", {"start": v(-141.18, 34.79) * mm, "end": v(-141.18, 29.79) * mm});
            skLineSegment(sketch, "E24.3.20.2", {"start": v(-146.18, 34.79) * mm, "end": v(-146.18, 29.79) * mm});
            skLineSegment(sketch, "E24.6.20.2", {"start": v(-146.18, 34.79) * mm, "end": v(-141.18, 34.79) * mm});
            skLineSegment(sketch, "E24.9.20.2", {"start": v(-146.18, 29.79) * mm, "end": v(-141.18, 29.79) * mm});
            skLineSegment(sketch, "E24.0.21.0", {"start": v(-133.18, 18.79) * mm, "end": v(-133.18, 13.79) * mm});
            skLineSegment(sketch, "E24.3.21.0", {"start": v(-138.18, 18.79) * mm, "end": v(-138.18, 13.79) * mm});
            skLineSegment(sketch, "E24.6.21.0", {"start": v(-138.18, 18.79) * mm, "end": v(-133.18, 18.79) * mm});
            skLineSegment(sketch, "E24.9.21.0", {"start": v(-138.18, 13.79) * mm, "end": v(-133.18, 13.79) * mm});
            skLineSegment(sketch, "E24.0.21.1", {"start": v(-133.18, 26.79) * mm, "end": v(-133.18, 21.79) * mm});
            skLineSegment(sketch, "E24.3.21.1", {"start": v(-138.18, 26.79) * mm, "end": v(-138.18, 21.79) * mm});
            skLineSegment(sketch, "E24.6.21.1", {"start": v(-138.18, 26.79) * mm, "end": v(-133.18, 26.79) * mm});
            skLineSegment(sketch, "E24.9.21.1", {"start": v(-138.18, 21.79) * mm, "end": v(-133.18, 21.79) * mm});
            skLineSegment(sketch, "E24.0.21.2", {"start": v(-133.18, 34.79) * mm, "end": v(-133.18, 29.79) * mm});
            skLineSegment(sketch, "E24.3.21.2", {"start": v(-138.18, 34.79) * mm, "end": v(-138.18, 29.79) * mm});
            skLineSegment(sketch, "E24.6.21.2", {"start": v(-138.18, 34.79) * mm, "end": v(-133.18, 34.79) * mm});
            skLineSegment(sketch, "E24.9.21.2", {"start": v(-138.18, 29.79) * mm, "end": v(-133.18, 29.79) * mm});
            skLineSegment(sketch, "E24.0.22.0", {"start": v(-125.18, 18.79) * mm, "end": v(-125.18, 13.79) * mm});
            skLineSegment(sketch, "E24.3.22.0", {"start": v(-130.18, 18.79) * mm, "end": v(-130.18, 13.79) * mm});
            skLineSegment(sketch, "E24.6.22.0", {"start": v(-130.18, 18.79) * mm, "end": v(-125.18, 18.79) * mm});
            skLineSegment(sketch, "E24.9.22.0", {"start": v(-130.18, 13.79) * mm, "end": v(-125.18, 13.79) * mm});
            skLineSegment(sketch, "E24.0.22.1", {"start": v(-125.18, 26.79) * mm, "end": v(-125.18, 21.79) * mm});
            skLineSegment(sketch, "E24.3.22.1", {"start": v(-130.18, 26.79) * mm, "end": v(-130.18, 21.79) * mm});
            skLineSegment(sketch, "E24.6.22.1", {"start": v(-130.18, 26.79) * mm, "end": v(-125.18, 26.79) * mm});
            skLineSegment(sketch, "E24.9.22.1", {"start": v(-130.18, 21.79) * mm, "end": v(-125.18, 21.79) * mm});
            skLineSegment(sketch, "E24.0.22.2", {"start": v(-125.18, 34.79) * mm, "end": v(-125.18, 29.79) * mm});
            skLineSegment(sketch, "E24.3.22.2", {"start": v(-130.18, 34.79) * mm, "end": v(-130.18, 29.79) * mm});
            skLineSegment(sketch, "E24.6.22.2", {"start": v(-130.18, 34.79) * mm, "end": v(-125.18, 34.79) * mm});
            skLineSegment(sketch, "E24.9.22.2", {"start": v(-130.18, 29.79) * mm, "end": v(-125.18, 29.79) * mm});
            skLineSegment(sketch, "E24.0.23.0", {"start": v(-117.18, 18.79) * mm, "end": v(-117.18, 13.79) * mm});
            skLineSegment(sketch, "E24.3.23.0", {"start": v(-122.18, 18.79) * mm, "end": v(-122.18, 13.79) * mm});
            skLineSegment(sketch, "E24.6.23.0", {"start": v(-122.18, 18.79) * mm, "end": v(-117.18, 18.79) * mm});
            skLineSegment(sketch, "E24.9.23.0", {"start": v(-122.18, 13.79) * mm, "end": v(-117.18, 13.79) * mm});
            skLineSegment(sketch, "E24.0.23.1", {"start": v(-117.18, 26.79) * mm, "end": v(-117.18, 21.79) * mm});
            skLineSegment(sketch, "E24.3.23.1", {"start": v(-122.18, 26.79) * mm, "end": v(-122.18, 21.79) * mm});
            skLineSegment(sketch, "E24.6.23.1", {"start": v(-122.18, 26.79) * mm, "end": v(-117.18, 26.79) * mm});
            skLineSegment(sketch, "E24.9.23.1", {"start": v(-122.18, 21.79) * mm, "end": v(-117.18, 21.79) * mm});
            skLineSegment(sketch, "E24.0.23.2", {"start": v(-117.18, 34.79) * mm, "end": v(-117.18, 29.79) * mm});
            skLineSegment(sketch, "E24.3.23.2", {"start": v(-122.18, 34.79) * mm, "end": v(-122.18, 29.79) * mm});
            skLineSegment(sketch, "E24.6.23.2", {"start": v(-122.18, 34.79) * mm, "end": v(-117.18, 34.79) * mm});
            skLineSegment(sketch, "E24.9.23.2", {"start": v(-122.18, 29.79) * mm, "end": v(-117.18, 29.79) * mm});
            skLineSegment(sketch, "E24.0.24.0", {"start": v(-109.18, 18.79) * mm, "end": v(-109.18, 13.79) * mm});
            skLineSegment(sketch, "E24.3.24.0", {"start": v(-114.18, 18.79) * mm, "end": v(-114.18, 13.79) * mm});
            skLineSegment(sketch, "E24.6.24.0", {"start": v(-114.18, 18.79) * mm, "end": v(-109.18, 18.79) * mm});
            skLineSegment(sketch, "E24.9.24.0", {"start": v(-114.18, 13.79) * mm, "end": v(-109.18, 13.79) * mm});
            skLineSegment(sketch, "E24.0.24.1", {"start": v(-109.18, 26.79) * mm, "end": v(-109.18, 21.79) * mm});
            skLineSegment(sketch, "E24.3.24.1", {"start": v(-114.18, 26.79) * mm, "end": v(-114.18, 21.79) * mm});
            skLineSegment(sketch, "E24.6.24.1", {"start": v(-114.18, 26.79) * mm, "end": v(-109.18, 26.79) * mm});
            skLineSegment(sketch, "E24.9.24.1", {"start": v(-114.18, 21.79) * mm, "end": v(-109.18, 21.79) * mm});
            skLineSegment(sketch, "E24.0.24.2", {"start": v(-109.18, 34.79) * mm, "end": v(-109.18, 29.79) * mm});
            skLineSegment(sketch, "E24.3.24.2", {"start": v(-114.18, 34.79) * mm, "end": v(-114.18, 29.79) * mm});
            skLineSegment(sketch, "E24.6.24.2", {"start": v(-114.18, 34.79) * mm, "end": v(-109.18, 34.79) * mm});
            skLineSegment(sketch, "E24.9.24.2", {"start": v(-114.18, 29.79) * mm, "end": v(-109.18, 29.79) * mm});
            skSolve(sketch);
        }
        {
            var Q0;
            Q0 = qSketchRegion(id + "F8", true);
            extrude(context, id + "F9", {"entities" : qUnion([Q0]), "operationType" : NewBodyOperationType.REMOVE, "oppositeDirection" : true, "depth" : 25 * mm});
        }
        {
            var Q0;
            Q0=makeQuery(id+"F3.opExtrude","CAP_FACE",FACE,{"disambiguationData":[OSD([sQuery(id+"F2.wireOp",EDGE,"E1.bottom"),sQuery(id+"F2.wireOp",EDGE,"E1.top"),sQuery(id+"F2.wireOp",EDGE,"E1.left"),sQuery(id+"F2.wireOp",EDGE,"E1.right")])],"isStart":false});
            var sketch = newSketch(context, id + "F10", { "sketchPlane" : qUnion([Q0])});
            skLineSegment(sketch, "E25", {"start": v(-99.18, 11.79) * mm, "end": v(-99.18, 95.79) * mm});
            skLineSegment(sketch, "E26", {"start": v(-99.18, 95.79) * mm, "end": v(-107.18, 103.79) * mm});
            skLineSegment(sketch, "E27", {"start": v(-107.18, 103.79) * mm, "end": v(-311.18, 103.79) * mm});
            skLineSegment(sketch, "E28", {"start": v(-311.18, 103.79) * mm, "end": v(-319.18, 95.79) * mm});
            skLineSegment(sketch, "E29", {"start": v(-319.18, 95.79) * mm, "end": v(-319.18, 11.79) * mm});
            skLineSegment(sketch, "E30", {"start": v(-306.18, 26.79) * mm, "end": v(-293.18, 13.79) * mm});
            skLineSegment(sketch, "E31", {"start": v(-293.18, 13.79) * mm, "end": v(-122.18, 13.79) * mm});
            skLineSegment(sketch, "E32", {"start": v(-122.18, 13.79) * mm, "end": v(-109.18, 26.79) * mm});
            skLineSegment(sketch, "E33", {"start": v(-109.18, 26.79) * mm, "end": v(-109.18, 34.79) * mm});
            skLineSegment(sketch, "E34", {"start": v(-109.18, 34.79) * mm, "end": v(-306.18, 34.79) * mm});
            skLineSegment(sketch, "E35", {"start": v(-306.18, 34.79) * mm, "end": v(-306.18, 26.79) * mm});
            skSolve(sketch);
        }
        {
            var Q0;
            Q0=makeQuery(id+"F10.imprint","IMPRINT",FACE,{"disambiguationData":[TD([[makeQuery(id+"F10.imprint","IMPRINT",EDGE,{"derivedFrom":sQuery(id+"F10.wireOp",EDGE,"E25")}),-1.0]])]});
            var Q1;
            {var subQ2=makeQuery(id+"F9.boolean.opBoolean","COPY",EDGE,{"derivedFrom":makeQuery(id+"F9.opExtrude","CAP_EDGE",EDGE,{"disambiguationData":[OSD([sQuery(id+"F8.wireOp",EDGE,"E23.0.1.1")])],"isStart":true})});Q1=makeQuery(id+"F10.imprint","IMPRINT",FACE,{"disambiguationData":[TD([[makeQuery(id+"F10.imprint","IMPRINT",EDGE,{"derivedFrom":subQ2}),1.0]])]});}
            var Q2;
            {var subQ2=makeQuery(id+"F9.boolean.opBoolean","COPY",EDGE,{"derivedFrom":makeQuery(id+"F9.opExtrude","CAP_EDGE",EDGE,{"disambiguationData":[OSD([sQuery(id+"F8.wireOp",EDGE,"E23.1.0.1")])],"isStart":true})});Q2=makeQuery(id+"F10.imprint","IMPRINT",FACE,{"disambiguationData":[TD([[makeQuery(id+"F10.imprint","IMPRINT",EDGE,{"derivedFrom":subQ2}),1.0]])]});}
            var Q3;
            Q3=makeQuery(id+"F10.imprint","IMPRINT",FACE,{"disambiguationData":[TD([[makeQuery(id+"F10.imprint","IMPRINT",EDGE,{"derivedFrom":makeQuery(id+"F9.boolean.opBoolean","COPY",EDGE,{"derivedFrom":makeQuery(id+"F9.opExtrude","CAP_EDGE",EDGE,{"disambiguationData":[OSD([sQuery(id+"F8.wireOp",EDGE,"E24.0.24.0")])],"isStart":true})})}),-1.0]])]});
            var Q4;
            {var subQ1=makeQuery(id+"F9.boolean.opBoolean","COPY",EDGE,{"derivedFrom":makeQuery(id+"F9.opExtrude","CAP_EDGE",EDGE,{"disambiguationData":[OSD([sQuery(id+"F8.wireOp",EDGE,"E24.0.24.1")])],"isStart":true})});Q4=makeQuery(id+"F10.imprint","IMPRINT",FACE,{"disambiguationData":[TD([[makeQuery(id+"F10.imprint","IMPRINT",EDGE,{"derivedFrom":subQ1}),-1.0]])]});}
            var Q5;
            Q5=makeQuery(id+"F10.imprint","IMPRINT",FACE,{"disambiguationData":[TD([[makeQuery(id+"F10.imprint","IMPRINT",EDGE,{"derivedFrom":makeQuery(id+"F9.boolean.opBoolean","COPY",EDGE,{"derivedFrom":makeQuery(id+"F9.opExtrude","CAP_EDGE",EDGE,{"disambiguationData":[OSD([sQuery(id+"F8.wireOp",EDGE,"E21.bottom")])],"isStart":true})})}),-1.0]])]});
            var Q6;
            {var subQ1=makeQuery(id+"F9.boolean.opBoolean","COPY",EDGE,{"derivedFrom":makeQuery(id+"F9.opExtrude","CAP_EDGE",EDGE,{"disambiguationData":[OSD([sQuery(id+"F8.wireOp",EDGE,"E24.0.23.0")])],"isStart":true})});Q6=makeQuery(id+"F10.imprint","IMPRINT",FACE,{"disambiguationData":[TD([[makeQuery(id+"F10.imprint","IMPRINT",EDGE,{"derivedFrom":subQ1}),-1.0]])]});}
            extrude(context, id + "F11", {"entities" : qUnion([Q0, Q1, Q2, Q3, Q4, Q5, Q6]), "operationType" : NewBodyOperationType.ADD, "oppositeDirection" : true, "depth" : 3 * mm});
        }
    });
